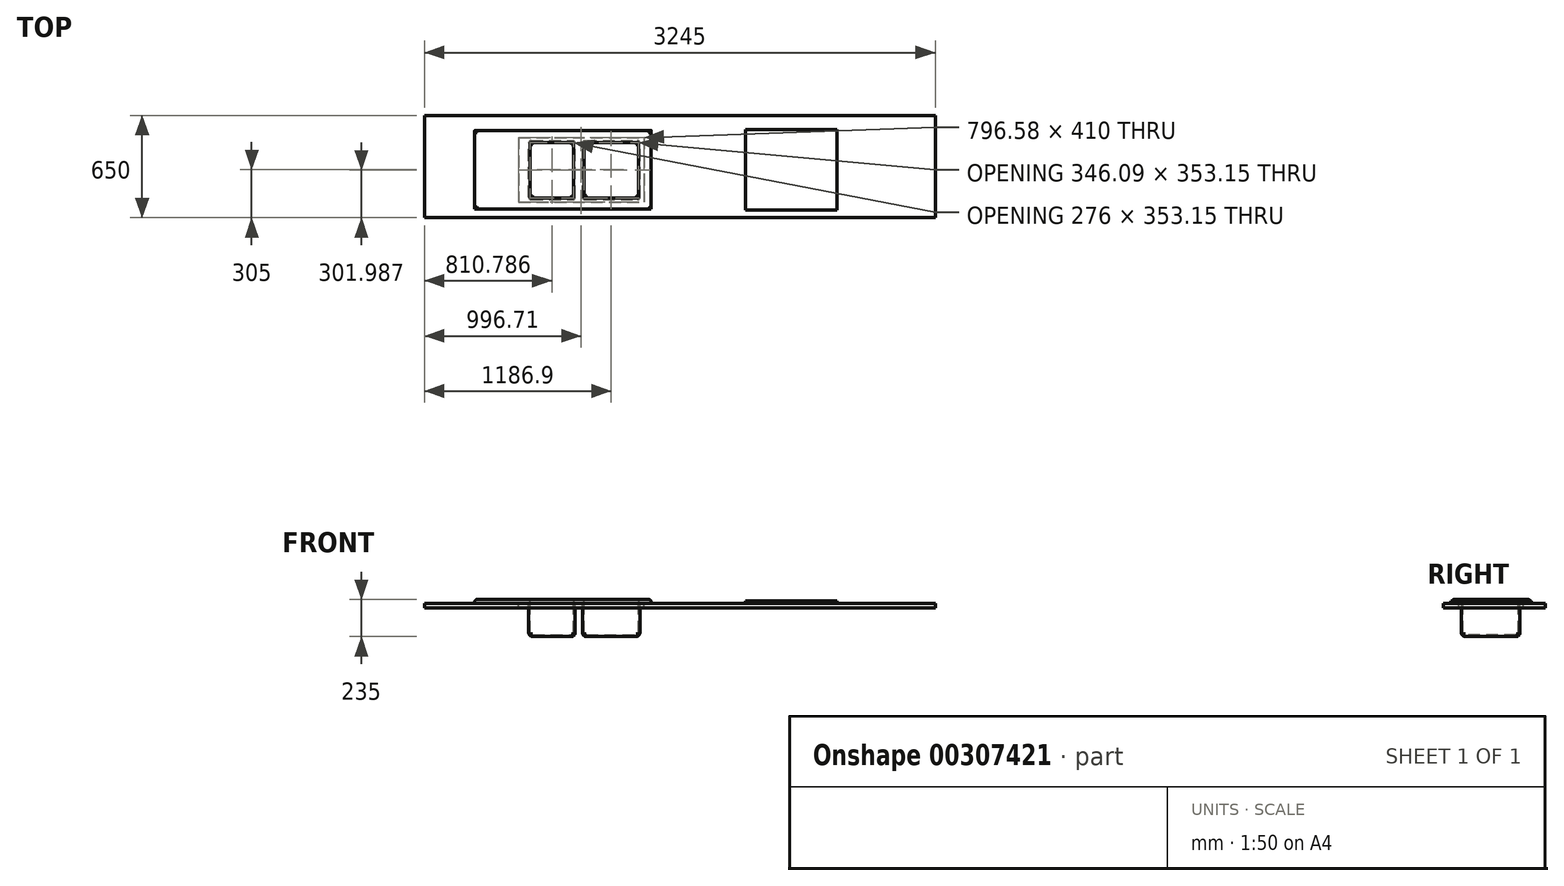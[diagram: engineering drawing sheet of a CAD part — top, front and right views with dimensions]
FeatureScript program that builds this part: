
annotation { "Feature Type Name" : "Feature", "Feature Type Description" : "" }
export const myFeature = defineFeature(function(context is Context, id is Id, definition is map)
    precondition{}
    {
        {
            var Q0;
            Q0=qCreatedBy(makeId("Top.planeOp"),FACE);
            var sketch = newSketch(context, id + "F0", { "sketchPlane" : qUnion([Q0])});
            skLineSegment(sketch, "E0.bottom", {"start": v(0, 0) * mm, "end": v(1120, 0) * mm});
            skLineSegment(sketch, "E0.top", {"start": v(0, -500) * mm, "end": v(1120, -500) * mm});
            skLineSegment(sketch, "E0.left", {"start": v(0, 0) * mm, "end": v(0, -500) * mm});
            skLineSegment(sketch, "E0.right", {"start": v(1120, 0) * mm, "end": v(1120, -500) * mm});
            skLineSegment(sketch, "E1.bottom", {"start": v(357.79, -76.44) * mm, "end": v(623.78, -76.44) * mm});
            skLineSegment(sketch, "E1.top", {"start": v(357.79, -429.59) * mm, "end": v(623.78, -429.59) * mm});
            skLineSegment(sketch, "E1.left", {"start": v(352.79, -81.44) * mm, "end": v(352.79, -424.59) * mm});
            skLineSegment(sketch, "E1.right", {"start": v(628.78, -81.44) * mm, "end": v(628.78, -424.59) * mm});
            skLineSegment(sketch, "E2.bottom", {"start": v(698.85, -76.44) * mm, "end": v(1034.94, -76.44) * mm});
            skLineSegment(sketch, "E2.top", {"start": v(698.85, -429.59) * mm, "end": v(1034.94, -429.59) * mm});
            skLineSegment(sketch, "E2.left", {"start": v(693.85, -81.44) * mm, "end": v(693.85, -424.59) * mm});
            skLineSegment(sketch, "E2.right", {"start": v(1039.94, -81.44) * mm, "end": v(1039.94, -424.59) * mm});
            skPoint(sketch, "E3.visualSharp", {"position": v(352.79, -76.44) * mm});
            skArc(sketch, "E3.filletArc", {"start": v(357.79, -76.44) * mm, "mid": v(354.25, -77.9) * mm, "end": v(352.79, -81.44) * mm});
            skPoint(sketch, "E4.visualSharp", {"position": v(352.79, -429.59) * mm});
            skArc(sketch, "E4.filletArc", {"start": v(352.79, -424.59) * mm, "mid": v(354.25, -428.13) * mm, "end": v(357.79, -429.59) * mm});
            skPoint(sketch, "E5.visualSharp", {"position": v(628.78, -429.59) * mm});
            skArc(sketch, "E5.filletArc", {"start": v(623.78, -429.59) * mm, "mid": v(627.32, -428.13) * mm, "end": v(628.78, -424.59) * mm});
            skPoint(sketch, "E6.visualSharp", {"position": v(628.78, -76.44) * mm});
            skArc(sketch, "E6.filletArc", {"start": v(628.78, -81.44) * mm, "mid": v(627.32, -77.9) * mm, "end": v(623.78, -76.44) * mm});
            skPoint(sketch, "E7.visualSharp", {"position": v(693.85, -76.44) * mm});
            skArc(sketch, "E7.filletArc", {"start": v(698.85, -76.44) * mm, "mid": v(695.32, -77.9) * mm, "end": v(693.85, -81.44) * mm});
            skPoint(sketch, "E8.visualSharp", {"position": v(693.85, -429.59) * mm});
            skArc(sketch, "E8.filletArc", {"start": v(693.85, -424.59) * mm, "mid": v(695.32, -428.13) * mm, "end": v(698.85, -429.59) * mm});
            skPoint(sketch, "E9.visualSharp", {"position": v(1039.94, -429.59) * mm});
            skArc(sketch, "E9.filletArc", {"start": v(1034.94, -429.59) * mm, "mid": v(1038.48, -428.13) * mm, "end": v(1039.94, -424.59) * mm});
            skPoint(sketch, "E10.visualSharp", {"position": v(1039.94, -76.44) * mm});
            skArc(sketch, "E10.filletArc", {"start": v(1039.94, -81.44) * mm, "mid": v(1038.48, -77.9) * mm, "end": v(1034.94, -76.44) * mm});
            skLineSegment(sketch, "E11.bottom", {"start": v(-320, 95) * mm, "end": v(2925, 95) * mm});
            skLineSegment(sketch, "E11.top", {"start": v(-320, -555) * mm, "end": v(2925, -555) * mm});
            skLineSegment(sketch, "E11.left", {"start": v(-320, 95) * mm, "end": v(-320, -555) * mm});
            skLineSegment(sketch, "E11.right", {"start": v(2925, 95) * mm, "end": v(2925, -555) * mm});
            skLineSegment(sketch, "E12.bottom", {"start": v(278.42, -45) * mm, "end": v(1075, -45) * mm});
            skLineSegment(sketch, "E12.top", {"start": v(278.42, -455) * mm, "end": v(1075, -455) * mm});
            skLineSegment(sketch, "E12.left", {"start": v(278.42, -45) * mm, "end": v(278.42, -455) * mm});
            skLineSegment(sketch, "E12.right", {"start": v(1075, -45) * mm, "end": v(1075, -455) * mm});
            skLineSegment(sketch, "E13.bottom", {"start": v(1720, -505) * mm, "end": v(2300, -505) * mm});
            skLineSegment(sketch, "E13.top", {"start": v(1720, 5) * mm, "end": v(2300, 5) * mm});
            skLineSegment(sketch, "E13.left", {"start": v(1720, -505) * mm, "end": v(1720, 5) * mm});
            skLineSegment(sketch, "E13.right", {"start": v(2300, -505) * mm, "end": v(2300, 5) * mm});
            skSolve(sketch);
        }
        {
            var Q0;
            Q0=makeQuery(id+"F0.imprint","IMPRINT",FACE,{"disambiguationData":[TD([[makeQuery(id+"F0.imprint","IMPRINT",EDGE,{"derivedFrom":sQuery(id+"F0.wireOp",EDGE,"E0.bottom")}),-1.0]])]});
            var Q1;
            Q1=makeQuery(id+"F0.imprint","IMPRINT",FACE,{"disambiguationData":[TD([[makeQuery(id+"F0.imprint","IMPRINT",EDGE,{"derivedFrom":sQuery(id+"F0.wireOp",EDGE,"E1.bottom")}),1.0]])]});
            extrude(context, id + "F1", {"entities" : qUnion([Q0, Q1]), "depth" : 25 * mm, "offsetDistance" : 25 * mm});
        }
        {
            var Q0;
            Q0=makeQuery(id+"F1.opExtrude","CAP_FACE",FACE,{"disambiguationData":[OSD([sQuery(id+"F0.wireOp",EDGE,"E0.bottom"),sQuery(id+"F0.wireOp",EDGE,"E0.top"),sQuery(id+"F0.wireOp",EDGE,"E0.left"),sQuery(id+"F0.wireOp",EDGE,"E0.right"),sQuery(id+"F0.wireOp",EDGE,"E1.bottom"),sQuery(id+"F0.wireOp",EDGE,"E1.top"),sQuery(id+"F0.wireOp",EDGE,"E1.left"),sQuery(id+"F0.wireOp",EDGE,"E1.right"),sQuery(id+"F0.wireOp",EDGE,"E2.bottom"),sQuery(id+"F0.wireOp",EDGE,"E2.top"),sQuery(id+"F0.wireOp",EDGE,"E2.left"),sQuery(id+"F0.wireOp",EDGE,"E2.right"),sQuery(id+"F0.wireOp",EDGE,"E3.filletArc"),sQuery(id+"F0.wireOp",EDGE,"E4.filletArc"),sQuery(id+"F0.wireOp",EDGE,"E5.filletArc"),sQuery(id+"F0.wireOp",EDGE,"E6.filletArc"),sQuery(id+"F0.wireOp",EDGE,"E7.filletArc"),sQuery(id+"F0.wireOp",EDGE,"E8.filletArc"),sQuery(id+"F0.wireOp",EDGE,"E9.filletArc"),sQuery(id+"F0.wireOp",EDGE,"E10.filletArc")])],"isStart":false});
            fillet(context, id + "F2", {"entities" : qUnion([Q0]), "radius" : 15 * mm, "tangentPropagation" : true, "allowEdgeOverflow" : false});
        }
        {
            var Q0;
            Q0=makeQuery(id+"F0.imprint","IMPRINT",FACE,{"disambiguationData":[TD([[makeQuery(id+"F0.imprint","IMPRINT",EDGE,{"derivedFrom":sQuery(id+"F0.wireOp",EDGE,"E1.bottom")}),-1.0]])]});
            var Q1;
            Q1=makeQuery(id+"F0.imprint","IMPRINT",FACE,{"disambiguationData":[TD([[makeQuery(id+"F0.imprint","IMPRINT",EDGE,{"derivedFrom":sQuery(id+"F0.wireOp",EDGE,"E2.bottom")}),-1.0]])]});
            extrude(context, id + "F3", {"entities" : qUnion([Q0, Q1]), "oppositeDirection" : true, "depth" : 200 * mm});
        }
        {
            var Q0;
            Q0=makeQuery(id+"F3.opExtrude","CAP_FACE",FACE,{"disambiguationData":[OSD([sQuery(id+"F0.wireOp",EDGE,"E1.bottom"),sQuery(id+"F0.wireOp",EDGE,"E1.top"),sQuery(id+"F0.wireOp",EDGE,"E1.left"),sQuery(id+"F0.wireOp",EDGE,"E1.right"),sQuery(id+"F0.wireOp",EDGE,"E3.filletArc"),sQuery(id+"F0.wireOp",EDGE,"E4.filletArc"),sQuery(id+"F0.wireOp",EDGE,"E5.filletArc"),sQuery(id+"F0.wireOp",EDGE,"E6.filletArc")])],"isStart":false});
            var Q1;
            Q1=makeQuery(id+"F3.opExtrude","CAP_FACE",FACE,{"disambiguationData":[OSD([sQuery(id+"F0.wireOp",EDGE,"E2.bottom"),sQuery(id+"F0.wireOp",EDGE,"E2.top"),sQuery(id+"F0.wireOp",EDGE,"E2.left"),sQuery(id+"F0.wireOp",EDGE,"E2.right"),sQuery(id+"F0.wireOp",EDGE,"E7.filletArc"),sQuery(id+"F0.wireOp",EDGE,"E8.filletArc"),sQuery(id+"F0.wireOp",EDGE,"E9.filletArc"),sQuery(id+"F0.wireOp",EDGE,"E10.filletArc")])],"isStart":false});
            fillet(context, id + "F4", {"entities" : qUnion([Q0, Q1]), "radius" : 15 * mm, "tangentPropagation" : true, "allowEdgeOverflow" : false});
        }
        {
            var Q0;
            Q0=makeQuery(id+"F3.opExtrude","CAP_FACE",FACE,{"disambiguationData":[OSD([sQuery(id+"F0.wireOp",EDGE,"E1.bottom"),sQuery(id+"F0.wireOp",EDGE,"E1.top"),sQuery(id+"F0.wireOp",EDGE,"E1.left"),sQuery(id+"F0.wireOp",EDGE,"E1.right"),sQuery(id+"F0.wireOp",EDGE,"E3.filletArc"),sQuery(id+"F0.wireOp",EDGE,"E4.filletArc"),sQuery(id+"F0.wireOp",EDGE,"E5.filletArc"),sQuery(id+"F0.wireOp",EDGE,"E6.filletArc")])],"isStart":true});
            var Q1;
            Q1=makeQuery(id+"F3.opExtrude","CAP_FACE",FACE,{"disambiguationData":[OSD([sQuery(id+"F0.wireOp",EDGE,"E2.bottom"),sQuery(id+"F0.wireOp",EDGE,"E2.top"),sQuery(id+"F0.wireOp",EDGE,"E2.left"),sQuery(id+"F0.wireOp",EDGE,"E2.right"),sQuery(id+"F0.wireOp",EDGE,"E7.filletArc"),sQuery(id+"F0.wireOp",EDGE,"E8.filletArc"),sQuery(id+"F0.wireOp",EDGE,"E9.filletArc"),sQuery(id+"F0.wireOp",EDGE,"E10.filletArc")])],"isStart":true});
            shell(context, id + "F5", {"entities" : qUnion([Q0, Q1]), "thickness" : 10 * mm, "oppositeDirection" : true});
        }
        {
            var Q0;
            Q0=makeQuery(id+"F0.imprint","IMPRINT",FACE,{"disambiguationData":[TD([[makeQuery(id+"F0.imprint","IMPRINT",EDGE,{"derivedFrom":sQuery(id+"F0.wireOp",EDGE,"E0.bottom")}),-1.0]])]});
            var Q1;
            Q1=makeQuery(id+"F0.imprint","IMPRINT",FACE,{"disambiguationData":[TD([[makeQuery(id+"F0.imprint","IMPRINT",EDGE,{"derivedFrom":sQuery(id+"F0.wireOp",EDGE,"E0.bottom")}),1.0]])]});
            var Q2;
            Q2=makeQuery(id+"F0.imprint","IMPRINT",FACE,{"disambiguationData":[TD([[makeQuery(id+"F0.imprint","IMPRINT",EDGE,{"derivedFrom":sQuery(id+"F0.wireOp",EDGE,"E13.bottom")}),1.0]])]});
            extrude(context, id + "F6", {"entities" : qUnion([Q0, Q1, Q2]), "oppositeDirection" : true, "depth" : 28 * mm, "offsetDistance" : 25 * mm});
        }
        {
            var Q0;
            Q0=makeQuery(id+"F0.imprint","IMPRINT",FACE,{"disambiguationData":[TD([[makeQuery(id+"F0.imprint","IMPRINT",EDGE,{"derivedFrom":sQuery(id+"F0.wireOp",EDGE,"E13.bottom")}),1.0]])]});
            extrude(context, id + "F7", {"entities" : qUnion([Q0]), "depth" : 15 * mm, "offsetDistance" : 25 * mm});
        }
    });
